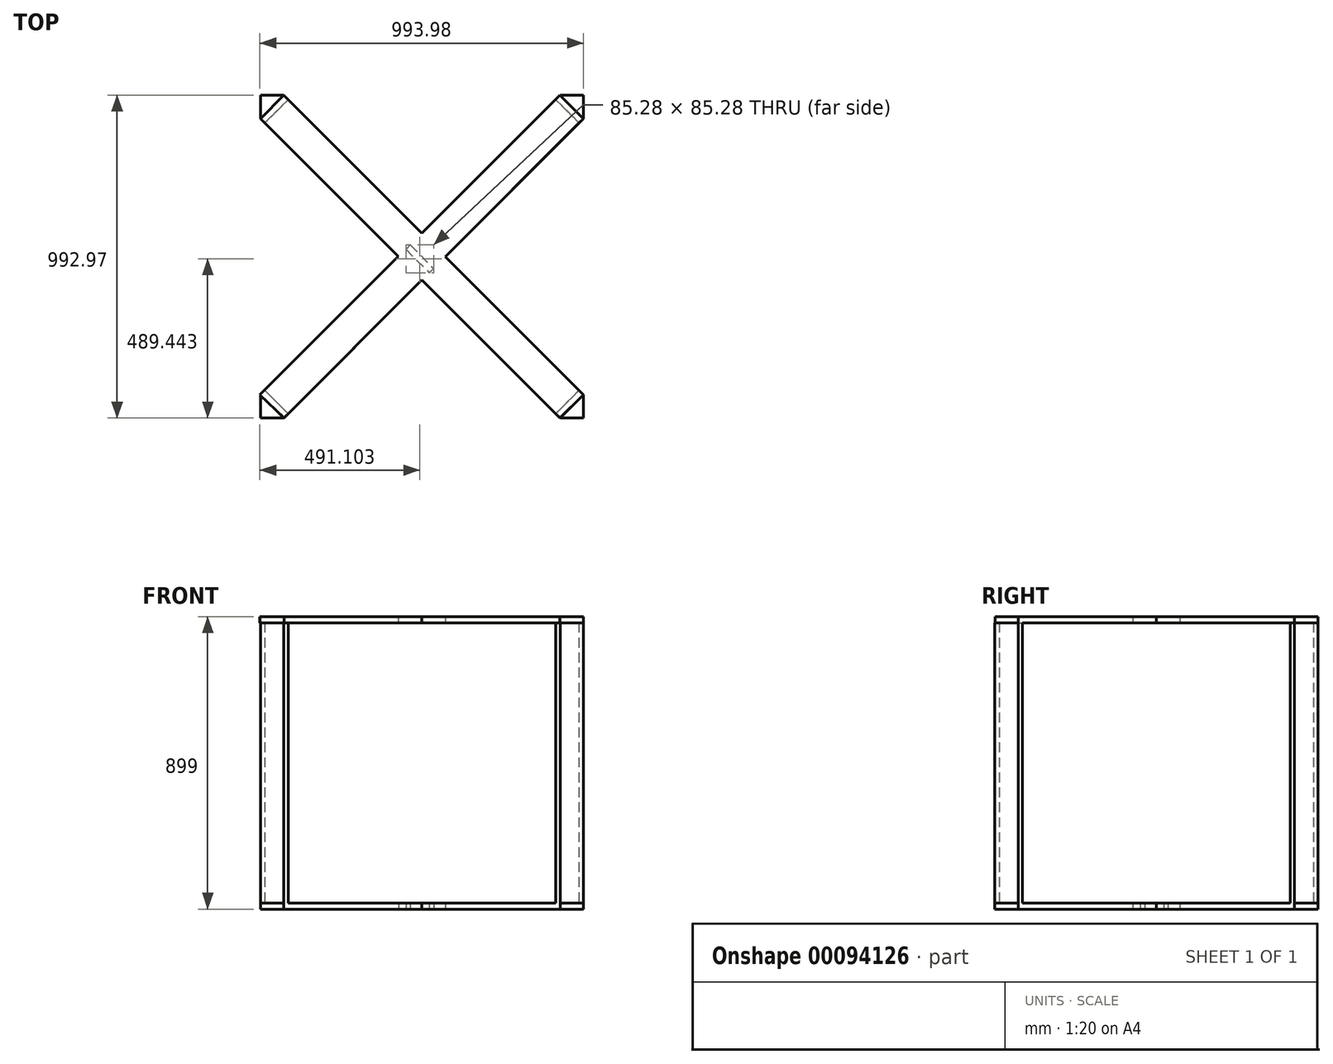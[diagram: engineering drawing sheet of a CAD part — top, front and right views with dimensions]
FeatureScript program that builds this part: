
annotation { "Feature Type Name" : "Feature", "Feature Type Description" : "" }
export const myFeature = defineFeature(function(context is Context, id is Id, definition is map)
    precondition{}
    {
        {
            var Q0;
            Q0=qCreatedBy(makeId("Top.planeOp"),FACE);
            var sketch = newSketch(context, id + "F0", { "sketchPlane" : qUnion([Q0])});
            skLineSegment(sketch, "E0.bottom", {"start": v(496.16, -496.16) * mm, "end": v(424.32, -496.16) * mm});
            skLineSegment(sketch, "E0.top", {"start": v(496.16, 496.16) * mm, "end": v(424.32, 496.16) * mm});
            skLineSegment(sketch, "E0.left", {"start": v(496.16, -496.16) * mm, "end": v(496.16, -424.32) * mm});
            skLineSegment(sketch, "E0.right", {"start": v(-496.16, -496.16) * mm, "end": v(-496.16, -424.32) * mm});
            skPoint(sketch, "E0.middle", {"position": v(0, 0) * mm});
            skLineSegment(sketch, "E1.0", {"start": v(-496.16, 424.32) * mm, "end": v(-71.84, 0) * mm});
            skLineSegment(sketch, "E2.0", {"start": v(-424.32, 496.16) * mm, "end": v(0, 71.84) * mm});
            skLineSegment(sketch, "E3.0", {"start": v(-424.32, -496.16) * mm, "end": v(496.16, 424.32) * mm});
            skLineSegment(sketch, "E4.0", {"start": v(-496.16, -424.32) * mm, "end": v(424.32, 496.16) * mm});
            skLineSegment(sketch, "E5.trimOffspring", {"start": v(71.84, 0) * mm, "end": v(496.16, -424.32) * mm});
            skLineSegment(sketch, "E6.trimOffspring", {"start": v(0, -71.84) * mm, "end": v(424.32, -496.16) * mm});
            skLineSegment(sketch, "E7.trimOffspring", {"start": v(-424.32, 496.16) * mm, "end": v(-496.16, 496.16) * mm});
            skLineSegment(sketch, "E8.trimOffspring", {"start": v(-496.16, 424.32) * mm, "end": v(-496.16, 496.16) * mm});
            skLineSegment(sketch, "E9.trimOffspring", {"start": v(-424.32, -496.16) * mm, "end": v(-496.16, -496.16) * mm});
            skLineSegment(sketch, "E10.trimOffspring", {"start": v(496.16, 424.32) * mm, "end": v(496.16, 496.16) * mm});
            skLineSegment(sketch, "E11", {"start": v(-496.16, -424.32) * mm, "end": v(-424.32, -496.16) * mm});
            skLineSegment(sketch, "E12", {"start": v(-424.32, -496.16) * mm, "end": v(-410.88, -482.72) * mm});
            skLineSegment(sketch, "E13", {"start": v(-496.16, -424.32) * mm, "end": v(-482.72, -410.88) * mm});
            skLineSegment(sketch, "E14", {"start": v(-482.72, -410.88) * mm, "end": v(-410.88, -482.72) * mm});
            skLineSegment(sketch, "E15", {"start": v(496.16, -424.32) * mm, "end": v(424.32, -496.16) * mm});
            skLineSegment(sketch, "E16", {"start": v(424.32, -496.16) * mm, "end": v(410.88, -482.72) * mm});
            skLineSegment(sketch, "E17", {"start": v(496.16, -424.32) * mm, "end": v(482.72, -410.88) * mm});
            skLineSegment(sketch, "E18", {"start": v(482.72, -410.88) * mm, "end": v(410.88, -482.72) * mm});
            skLineSegment(sketch, "E19", {"start": v(496.16, 424.32) * mm, "end": v(424.32, 496.16) * mm});
            skLineSegment(sketch, "E20", {"start": v(424.32, 496.16) * mm, "end": v(410.88, 482.72) * mm});
            skLineSegment(sketch, "E21", {"start": v(410.88, 482.72) * mm, "end": v(482.72, 410.88) * mm});
            skLineSegment(sketch, "E22", {"start": v(482.72, 410.88) * mm, "end": v(496.16, 424.32) * mm});
            skLineSegment(sketch, "E23", {"start": v(-424.32, 496.16) * mm, "end": v(-496.16, 424.32) * mm});
            skLineSegment(sketch, "E24", {"start": v(-496.16, 424.32) * mm, "end": v(-482.72, 410.88) * mm});
            skLineSegment(sketch, "E25", {"start": v(-482.72, 410.88) * mm, "end": v(-410.88, 482.72) * mm});
            skLineSegment(sketch, "E26", {"start": v(-410.88, 482.72) * mm, "end": v(-424.32, 496.16) * mm});
            skLineSegment(sketch, "E27", {"start": v(0, 0) * mm, "end": v(35.92, -35.92) * mm});
            skLineSegment(sketch, "E28", {"start": v(35.92, -35.92) * mm, "end": v(-35.92, 35.92) * mm});
            skLineSegment(sketch, "E29", {"start": v(-35.92, 35.92) * mm, "end": v(-49.36, 22.49) * mm});
            skLineSegment(sketch, "E30", {"start": v(-49.36, 22.49) * mm, "end": v(22.49, -49.36) * mm});
            skSolve(sketch);
        }
        {
            var Q0;
            Q0 = qSketchRegion(id + "F0", true);
            extrude(context, id + "F1", {"entities" : qUnion([Q0]), "depth" : 19 * mm});
        }
        {
            var Q0;
            {var subQ0=sQuery(id+"F0.wireOp",EDGE,"E29");Q0=makeQuery(id+"F0.imprint","IMPRINT",FACE,{"disambiguationData":[TD([[makeQuery(id+"F0.imprint","IMPRINT",EDGE,{"derivedFrom":subQ0}),1.0]])]});}
            var Q1;
            Q1=makeQuery(id+"F0.imprint","IMPRINT",FACE,{"disambiguationData":[TD([[makeQuery(id+"F0.imprint","IMPRINT",EDGE,{"derivedFrom":sQuery(id+"F0.wireOp",EDGE,"E15")}),-1.0]])]});
            var Q2;
            Q2=makeQuery(id+"F0.imprint","IMPRINT",FACE,{"disambiguationData":[TD([[makeQuery(id+"F0.imprint","IMPRINT",EDGE,{"derivedFrom":sQuery(id+"F0.wireOp",EDGE,"E11")}),1.0]])]});
            var Q3;
            Q3=makeQuery(id+"F0.imprint","IMPRINT",FACE,{"disambiguationData":[TD([[makeQuery(id+"F0.imprint","IMPRINT",EDGE,{"derivedFrom":sQuery(id+"F0.wireOp",EDGE,"E19")}),1.0]])]});
            var Q4;
            Q4=makeQuery(id+"F0.imprint","IMPRINT",FACE,{"disambiguationData":[TD([[makeQuery(id+"F0.imprint","IMPRINT",EDGE,{"derivedFrom":sQuery(id+"F0.wireOp",EDGE,"E23")}),1.0]])]});
            extrude(context, id + "F2", {"entities" : qUnion([Q0, Q1, Q2, Q3, Q4]), "operationType" : NewBodyOperationType.ADD, "depth" : 880 * mm});
        }
        {
            var Q0;
            Q0=makeQuery(id+"F2.opExtrude","CAP_FACE",FACE,{"disambiguationData":[OSD([sQuery(id+"F0.wireOp",EDGE,"E23"),sQuery(id+"F0.wireOp",EDGE,"E24"),sQuery(id+"F0.wireOp",EDGE,"E25"),sQuery(id+"F0.wireOp",EDGE,"E26")])],"isStart":false});
            var sketch = newSketch(context, id + "F3", { "sketchPlane" : qUnion([Q0])});
            skLineSegment(sketch, "E31", {"start": v(-424.32, 496.16) * mm, "end": v(495.8, -423.96) * mm});
            skLineSegment(sketch, "E32", {"start": v(495.8, -423.96) * mm, "end": v(424.02, -495.73) * mm});
            skLineSegment(sketch, "E33", {"start": v(424.02, -495.73) * mm, "end": v(-496.16, 424.32) * mm});
            skLineSegment(sketch, "E34", {"start": v(-496.16, 424.32) * mm, "end": v(-424.32, 496.16) * mm});
            skLineSegment(sketch, "E35", {"start": v(-423.77, -495.61) * mm, "end": v(496.1, 424.41) * mm});
            skLineSegment(sketch, "E36", {"start": v(496.1, 424.41) * mm, "end": v(423.69, 496.81) * mm});
            skLineSegment(sketch, "E37", {"start": v(423.69, 496.81) * mm, "end": v(-497.82, -424.82) * mm});
            skLineSegment(sketch, "E38", {"start": v(-497.82, -424.82) * mm, "end": v(-423.77, -495.61) * mm});
            skSolve(sketch);
        }
        {
            var Q0;
            Q0 = qSketchRegion(id + "F3", true);
            extrude(context, id + "F4", {"entities" : qUnion([Q0]), "operationType" : NewBodyOperationType.ADD, "depth" : 19 * mm});
        }
    });
